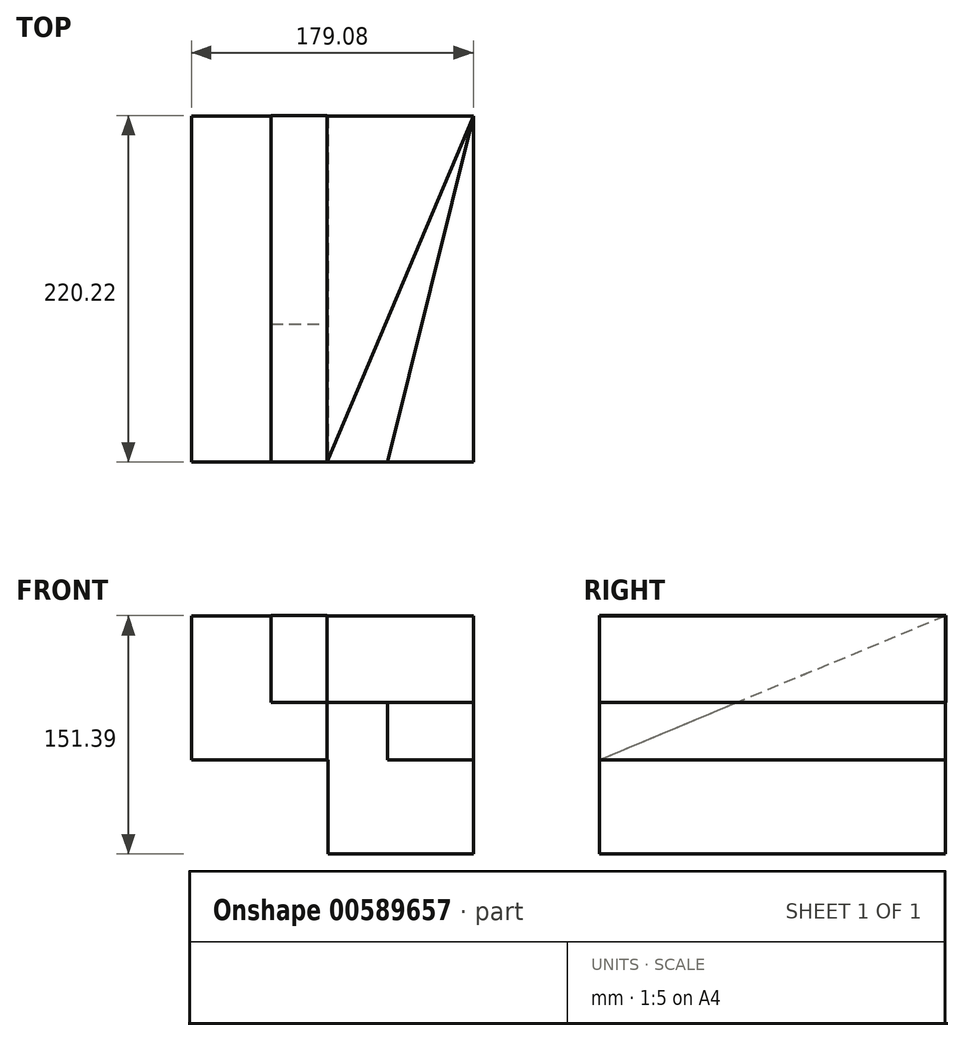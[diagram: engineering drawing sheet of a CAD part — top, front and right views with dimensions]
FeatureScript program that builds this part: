
annotation { "Feature Type Name" : "Feature", "Feature Type Description" : "" }
export const myFeature = defineFeature(function(context is Context, id is Id, definition is map)
    precondition{}
    {
        {
            var Q0;
            Q0=qCreatedBy(makeId("Front.planeOp"),FACE);
            var sketch = newSketch(context, id + "F0", { "sketchPlane" : qUnion([Q0])});
            skLineSegment(sketch, "E0.bottom", {"start": v(0, 0) * mm, "end": v(92.94, 0) * mm});
            skLineSegment(sketch, "E0.top", {"start": v(0, 151.24) * mm, "end": v(92.94, 151.24) * mm});
            skLineSegment(sketch, "E0.left", {"start": v(0, 0) * mm, "end": v(0, 151.24) * mm});
            skLineSegment(sketch, "E0.right", {"start": v(92.94, 0) * mm, "end": v(92.94, 151.24) * mm});
            skSolve(sketch);
        }
        {
            var Q0;
            Q0=makeQuery(id+"F0.imprint","IMPRINT",FACE,{"disambiguationData":[TD([[makeQuery(id+"F0.imprint","IMPRINT",EDGE,{"derivedFrom":sQuery(id+"F0.wireOp",EDGE,"E0.bottom")}),1.0]])]});
            extrude(context, id + "F1", {"entities" : qUnion([Q0]), "depth" : 219.72 * mm, "offsetDistance" : 25.4 * mm});
        }
        {
            var Q0;
            Q0=makeQuery(id+"F1.opExtrude","SWEPT_FACE",FACE,{"disambiguationData":[OSD([sQuery(id+"F0.wireOp",EDGE,"E0.top")])]});
            var sketch = newSketch(context, id + "F2", { "sketchPlane" : qUnion([Q0])});
            skLineSegment(sketch, "E1", {"start": v(92.94, 0) * mm, "end": v(0, -219.72) * mm});
            skLineSegment(sketch, "E2", {"start": v(0, -219.72) * mm, "end": v(121.03, -270.91) * mm});
            skLineSegment(sketch, "E3", {"start": v(121.03, -270.91) * mm, "end": v(220.06, -36.8) * mm});
            skLineSegment(sketch, "E4", {"start": v(220.06, -36.8) * mm, "end": v(92.94, 0) * mm});
            skSolve(sketch);
        }
        {
            var Q0;
            Q0=makeQuery(id+"F2.imprint","IMPRINT",FACE,{"disambiguationData":[TD([[makeQuery(id+"F2.imprint","IMPRINT",EDGE,{"derivedFrom":sQuery(id+"F2.wireOp",EDGE,"E1")}),1.0]])]});
            extrude(context, id + "F3", {"entities" : qUnion([Q0]), "operationType" : NewBodyOperationType.REMOVE, "oppositeDirection" : true, "depth" : 55.02 * mm, "offsetDistance" : 25.4 * mm});
        }
        {
            var Q0;
            Q0=makeQuery(id+"F1.opExtrude","SWEPT_FACE",FACE,{"disambiguationData":[OSD([sQuery(id+"F0.wireOp",EDGE,"E0.left")])]});
            extrude(context, id + "F4", {"entities" : qUnion([Q0]), "operationType" : NewBodyOperationType.ADD, "depth" : 86.14 * mm, "offsetDistance" : 25.4 * mm});
        }
        {
            var Q0;
            Q0=makeQuery(id+"F3.boolean.opBoolean","COPY",FACE,{"derivedFrom":makeQuery(id+"F3.opExtrude","CAP_FACE",FACE,{"disambiguationData":[OSD([sQuery(id+"F0.wireOp",EDGE,"E0.top"),sQuery(id+"F0.wireOp",EDGE,"E0.right"),sQuery(id+"F2.wireOp",EDGE,"E1")])],"isStart":false})});
            var sketch = newSketch(context, id + "F5", { "sketchPlane" : qUnion([Q0])});
            skLineSegment(sketch, "E5", {"start": v(92.94, 0) * mm, "end": v(31.38, -248.42) * mm});
            skLineSegment(sketch, "E6", {"start": v(31.38, -248.42) * mm, "end": v(158.6, -248.42) * mm});
            skLineSegment(sketch, "E7", {"start": v(158.6, -248.42) * mm, "end": v(158.6, 33) * mm});
            skLineSegment(sketch, "E8", {"start": v(158.6, 33) * mm, "end": v(92.94, 0) * mm});
            skSolve(sketch);
        }
        {
            var Q0;
            Q0 = qSketchRegion(id + "F5", true);
            var Q1;
            {var subQ0=sQuery(id+"F5.wireOp",EDGE,"E6");Q1=makeQuery(id+"F5.imprint","IMPRINT",FACE,{"disambiguationData":[TD([[makeQuery(id+"F5.imprint","IMPRINT",EDGE,{"derivedFrom":subQ0}),1.0]])]});}
            extrude(context, id + "F6", {"entities" : qUnion([Q0, Q1]), "operationType" : NewBodyOperationType.REMOVE, "oppositeDirection" : true, "depth" : 36.56 * mm, "offsetDistance" : 25.4 * mm});
        }
        {
            var Q0;
            Q0=makeQuery(id+"F4.opExtrude","CAP_FACE",FACE,{"disambiguationData":[OSD([sQuery(id+"F0.wireOp",EDGE,"E0.left")])],"isStart":false});
            var sketch = newSketch(context, id + "F7", { "sketchPlane" : qUnion([Q0])});
            skLineSegment(sketch, "E9", {"start": v(0, 151.24) * mm, "end": v(247.87, 54.02) * mm});
            skLineSegment(sketch, "E10", {"start": v(247.87, 54.02) * mm, "end": v(303.4, 195.57) * mm});
            skLineSegment(sketch, "E11", {"start": v(303.4, 195.57) * mm, "end": v(29.38, 269.22) * mm});
            skLineSegment(sketch, "E12", {"start": v(29.38, 269.22) * mm, "end": v(0, 151.24) * mm});
            skSolve(sketch);
        }
        {
            var Q0;
            {var subQ0=sQuery(id+"F7.wireOp",EDGE,"E10");Q0=makeQuery(id+"F7.imprint","IMPRINT",FACE,{"disambiguationData":[TD([[makeQuery(id+"F7.imprint","IMPRINT",EDGE,{"derivedFrom":subQ0}),1.0]])]});}
            extrude(context, id + "F8", {"entities" : qUnion([Q0]), "operationType" : NewBodyOperationType.REMOVE, "oppositeDirection" : true, "depth" : 101.38 * mm, "offsetDistance" : 25.4 * mm});
        }
        {
            var Q0;
            {var subQ0=sQuery(id+"F0.wireOp",EDGE,"E0.left");var subQ1=sQuery(id+"F0.wireOp",EDGE,"E0.top");Q0=makeQuery(id+"F4.boolean.opBoolean","MERGE",FACE,{"derivedFrom":[makeQuery(id+"F1.opExtrude","CAP_FACE",FACE,{"disambiguationData":[OSD([sQuery(id+"F0.wireOp",EDGE,"E0.bottom"),subQ1,subQ0,sQuery(id+"F0.wireOp",EDGE,"E0.right")])],"isStart":false}),makeQuery(id+"F4.opExtrude","SWEPT_FACE",FACE,{"disambiguationData":[OSD([subQ1,subQ0,sQuery(id+"F2.wireOp",EDGE,"E1"),sQuery(id+"F2.wireOp",EDGE,"E2")])]})]});}
            var sketch = newSketch(context, id + "F9", { "sketchPlane" : qUnion([Q0])});
            skLineSegment(sketch, "E13.bottom", {"start": v(-86.14, 0) * mm, "end": v(0.7, 0) * mm});
            skLineSegment(sketch, "E13.top", {"start": v(-86.14, 59.66) * mm, "end": v(0.7, 59.66) * mm});
            skLineSegment(sketch, "E13.left", {"start": v(-86.14, 0) * mm, "end": v(-86.14, 59.66) * mm});
            skLineSegment(sketch, "E13.right", {"start": v(0.7, 0) * mm, "end": v(0.7, 59.66) * mm});
            skSolve(sketch);
        }
        {
            var Q0;
            Q0 = qSketchRegion(id + "F9", true);
            extrude(context, id + "F10", {"entities" : qUnion([Q0]), "operationType" : NewBodyOperationType.REMOVE, "oppositeDirection" : true, "depth" : 283.97 * mm, "offsetDistance" : 25.4 * mm});
        }
        {
            var Q0;
            Q0=makeQuery(id+"F4.opExtrude","CAP_FACE",FACE,{"disambiguationData":[OSD([sQuery(id+"F0.wireOp",EDGE,"E0.left")])],"isStart":false});
            var sketch = newSketch(context, id + "F11", { "sketchPlane" : qUnion([Q0])});
            skLineSegment(sketch, "E14", {"start": v(0, 151.24) * mm, "end": v(219.72, 59.66) * mm});
            skLineSegment(sketch, "E15", {"start": v(219.72, 59.66) * mm, "end": v(219.72, 151.24) * mm});
            skLineSegment(sketch, "E16", {"start": v(219.72, 151.24) * mm, "end": v(0, 151.24) * mm});
            skSolve(sketch);
        }
        {
            var Q0;
            Q0=makeQuery(id+"F11.imprint","IMPRINT",FACE,{"disambiguationData":[TD([[makeQuery(id+"F11.imprint","IMPRINT",EDGE,{"derivedFrom":sQuery(id+"F11.wireOp",EDGE,"E14")}),1.0]])]});
            extrude(context, id + "F12", {"entities" : qUnion([Q0]), "operationType" : NewBodyOperationType.REMOVE, "oppositeDirection" : true, "depth" : 86.1 * mm, "offsetDistance" : 25.4 * mm});
        }
        {
            var Q0;
            {var subQ0=sQuery(id+"F0.wireOp",EDGE,"E0.left");var subQ1=sQuery(id+"F0.wireOp",EDGE,"E0.top");Q0=makeQuery(id+"F4.boolean.opBoolean","MERGE",FACE,{"derivedFrom":[makeQuery(id+"F1.opExtrude","CAP_FACE",FACE,{"disambiguationData":[OSD([sQuery(id+"F0.wireOp",EDGE,"E0.bottom"),subQ1,subQ0,sQuery(id+"F0.wireOp",EDGE,"E0.right")])],"isStart":false}),makeQuery(id+"F4.opExtrude","SWEPT_FACE",FACE,{"disambiguationData":[OSD([subQ1,subQ0,sQuery(id+"F2.wireOp",EDGE,"E1"),sQuery(id+"F2.wireOp",EDGE,"E2")])]})]});}
            var sketch = newSketch(context, id + "F13", { "sketchPlane" : qUnion([Q0])});
            skLineSegment(sketch, "E17.bottom", {"start": v(0, 96.22) * mm, "end": v(-35.5, 96.22) * mm});
            skLineSegment(sketch, "E17.top", {"start": v(0, 151.39) * mm, "end": v(-35.5, 151.39) * mm});
            skLineSegment(sketch, "E17.left", {"start": v(0, 96.22) * mm, "end": v(0, 151.39) * mm});
            skLineSegment(sketch, "E17.right", {"start": v(-35.5, 96.22) * mm, "end": v(-35.5, 151.39) * mm});
            skSolve(sketch);
        }
        {
            var Q0;
            {var subQ3=sQuery(id+"F13.wireOp",EDGE,"E17.top");Q0=makeQuery(id+"F13.imprint","IMPRINT",FACE,{"disambiguationData":[TD([[makeQuery(id+"F13.imprint","IMPRINT",EDGE,{"derivedFrom":subQ3}),1.0]])]});}
            extrude(context, id + "F14", {"entities" : qUnion([Q0]), "operationType" : NewBodyOperationType.ADD, "oppositeDirection" : true, "depth" : 220.22 * mm, "offsetDistance" : 25.4 * mm});
        }
    });
